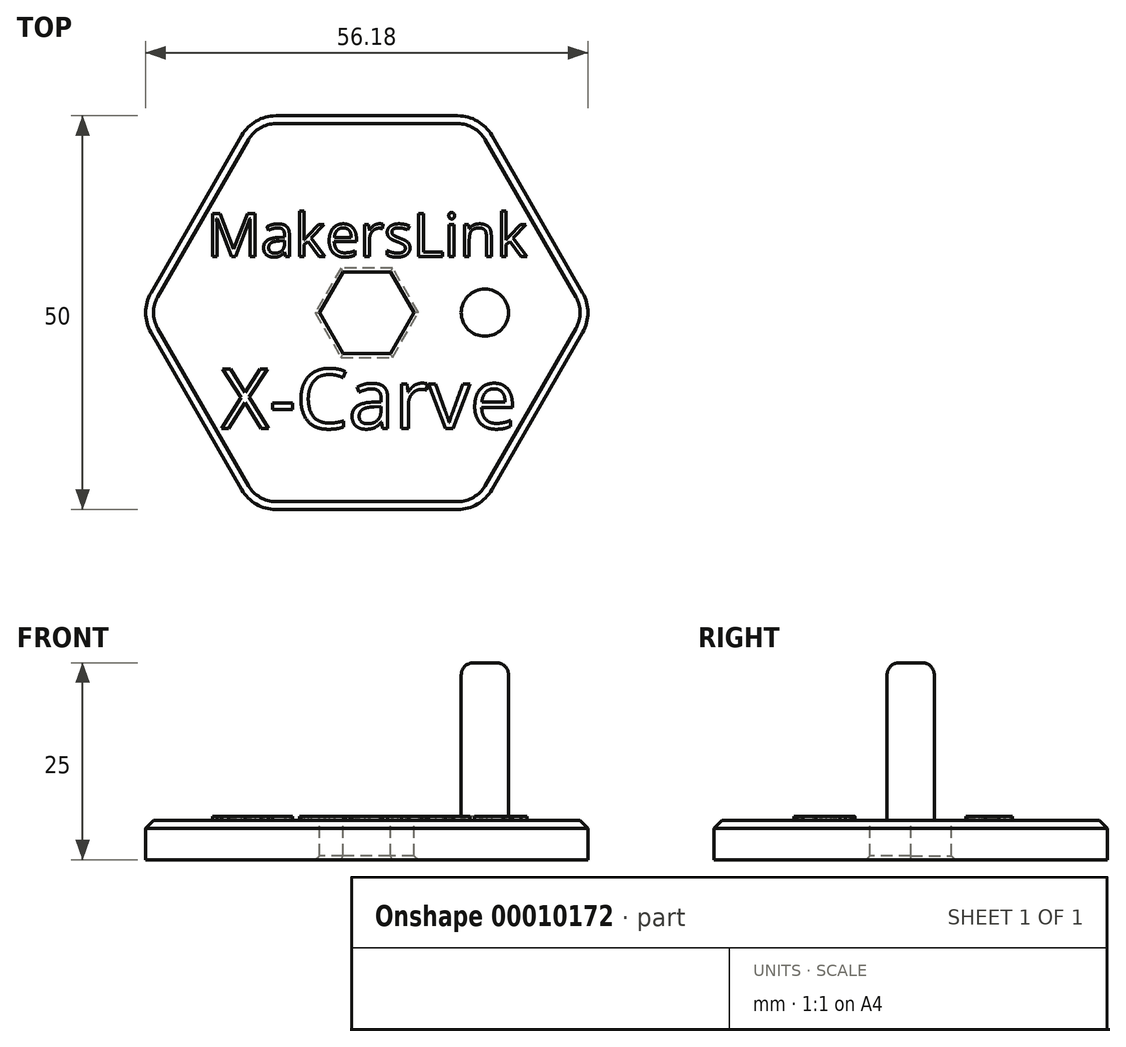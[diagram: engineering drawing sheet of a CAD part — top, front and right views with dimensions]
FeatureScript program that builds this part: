
annotation { "Feature Type Name" : "Feature", "Feature Type Description" : "" }
export const myFeature = defineFeature(function(context is Context, id is Id, definition is map)
    precondition{}
    {
        {
            var Q0;
            Q0=qCreatedBy(makeId("Top.planeOp"),FACE);
            var sketch = newSketch(context, id + "F0", { "sketchPlane" : qUnion([Q0])});
            skCircle(sketch, "E0.cCircle", {"center": v(0, 0) * mm, "radius": 5.17 * mm, "construction": true});
            skLineSegment(sketch, "E0.0", {"start": v(2.99, -5.17) * mm, "end": v(-2.99, -5.17) * mm});
            skLineSegment(sketch, "E0.1", {"start": v(-2.99, -5.17) * mm, "end": v(-5.98, 0) * mm});
            skLineSegment(sketch, "E0.2", {"start": v(-5.98, 0) * mm, "end": v(-2.99, 5.18) * mm});
            skLineSegment(sketch, "E0.3", {"start": v(-2.99, 5.17) * mm, "end": v(2.99, 5.18) * mm});
            skLineSegment(sketch, "E0.4", {"start": v(2.99, 5.18) * mm, "end": v(5.98, 0) * mm});
            skLineSegment(sketch, "E0.5", {"start": v(5.98, 0) * mm, "end": v(2.99, -5.17) * mm});
            skPoint(sketch, "E0.0.midPoint", {"position": v(0, -5.17) * mm});
            skCircle(sketch, "E1.cCircle", {"center": v(0, 0) * mm, "radius": 25 * mm, "construction": true});
            skLineSegment(sketch, "E1.0", {"start": v(14.43, -25) * mm, "end": v(-14.43, -25) * mm});
            skLineSegment(sketch, "E1.1", {"start": v(-14.43, -25) * mm, "end": v(-28.87, 0) * mm});
            skLineSegment(sketch, "E1.2", {"start": v(-28.87, 0) * mm, "end": v(-14.43, 25) * mm});
            skLineSegment(sketch, "E1.3", {"start": v(-14.43, 25) * mm, "end": v(14.43, 25) * mm});
            skLineSegment(sketch, "E1.4", {"start": v(14.43, 25) * mm, "end": v(28.87, 0) * mm});
            skLineSegment(sketch, "E1.5", {"start": v(28.87, 0) * mm, "end": v(14.43, -25) * mm});
            skPoint(sketch, "E1.0.midPoint", {"position": v(0, -25) * mm});
            skSolve(sketch);
        }
        {
            var Q0;
            Q0 = qSketchRegion(id + "F0", true);
            extrude(context, id + "F1", {"entities" : qUnion([Q0]), "oppositeDirection" : true, "depth" : 5 * mm});
        }
        {
            var Q0;
            Q0=makeQuery(id+"F1.opExtrude","CAP_FACE",FACE,{"disambiguationData":[OSD([sQuery(id+"F0.wireOp",EDGE,"E0.0"),sQuery(id+"F0.wireOp",EDGE,"E0.1"),sQuery(id+"F0.wireOp",EDGE,"E0.2"),sQuery(id+"F0.wireOp",EDGE,"E0.3"),sQuery(id+"F0.wireOp",EDGE,"E0.4"),sQuery(id+"F0.wireOp",EDGE,"E0.5"),sQuery(id+"F0.wireOp",EDGE,"E1.0"),sQuery(id+"F0.wireOp",EDGE,"E1.1"),sQuery(id+"F0.wireOp",EDGE,"E1.2"),sQuery(id+"F0.wireOp",EDGE,"E1.3"),sQuery(id+"F0.wireOp",EDGE,"E1.4"),sQuery(id+"F0.wireOp",EDGE,"E1.5")])],"isStart":true});
            var sketch = newSketch(context, id + "F2", { "sketchPlane" : qUnion([Q0])});
            skText(sketch, "E2", { "text": "X-Carve", "fontName": "OpenSans-Regular.ttf"});
            skText(sketch, "E3", { "text": "MakersLink", "fontName": "OpenSans-Regular.ttf"});
            const initialGuessF2  = {"E2": [-0.0185, -0.01472, 1, 0, 0.0076], "E3": [-0.02036, 0.00712, 1, 0, 0.0055]};
            skSetInitialGuess(sketch, initialGuessF2);
            skSolve(sketch);
        }
        {
            var Q0;
            Q0 = qSketchRegion(id + "F2", true);
            extrude(context, id + "F3", {"entities" : qUnion([Q0]), "operationType" : NewBodyOperationType.ADD, "depth" : 0.5 * mm});
        }
        {
            var Q0;
            Q0=makeQuery(id+"F1.opExtrude","SWEPT_EDGE",EDGE,{"disambiguationData":[OSD([sQuery(id+"F0.wireOp",EDGE,"E1.3"),sQuery(id+"F0.wireOp",EDGE,"E1.4")])]});
            var Q1;
            Q1=makeQuery(id+"F1.opExtrude","SWEPT_EDGE",EDGE,{"disambiguationData":[OSD([sQuery(id+"F0.wireOp",EDGE,"E1.4"),sQuery(id+"F0.wireOp",EDGE,"E1.5")])]});
            var Q2;
            Q2=makeQuery(id+"F1.opExtrude","SWEPT_EDGE",EDGE,{"disambiguationData":[OSD([sQuery(id+"F0.wireOp",EDGE,"E1.0"),sQuery(id+"F0.wireOp",EDGE,"E1.5")])]});
            var Q3;
            Q3=makeQuery(id+"F1.opExtrude","SWEPT_EDGE",EDGE,{"disambiguationData":[OSD([sQuery(id+"F0.wireOp",EDGE,"E1.0"),sQuery(id+"F0.wireOp",EDGE,"E1.1")])]});
            var Q4;
            Q4=makeQuery(id+"F1.opExtrude","SWEPT_EDGE",EDGE,{"disambiguationData":[OSD([sQuery(id+"F0.wireOp",EDGE,"E1.1"),sQuery(id+"F0.wireOp",EDGE,"E1.2")])]});
            var Q5;
            Q5=makeQuery(id+"F1.opExtrude","SWEPT_EDGE",EDGE,{"disambiguationData":[OSD([sQuery(id+"F0.wireOp",EDGE,"E1.2"),sQuery(id+"F0.wireOp",EDGE,"E1.3")])]});
            fillet(context, id + "F4", {"entities" : qUnion([Q0, Q1, Q2, Q3, Q4, Q5]), "radius" : 5 * mm, "tangentPropagation" : true, "allowEdgeOverflow" : false});
        }
        {
            var Q0;
            Q0=makeQuery(id+"F1.opExtrude","CAP_EDGE",EDGE,{"disambiguationData":[OSD([sQuery(id+"F0.wireOp",EDGE,"E1.3")])],"isStart":true});
            var Q1;
            Q1=makeQuery(id+"F1.opExtrude","CAP_EDGE",EDGE,{"disambiguationData":[OSD([sQuery(id+"F0.wireOp",EDGE,"E1.2")])],"isStart":true});
            var Q2;
            Q2=makeQuery(id+"F1.opExtrude","CAP_EDGE",EDGE,{"disambiguationData":[OSD([sQuery(id+"F0.wireOp",EDGE,"E1.1")])],"isStart":true});
            var Q3;
            {var subQ0=sQuery(id+"F0.wireOp",EDGE,"E1.1");var subQ1=sQuery(id+"F0.wireOp",EDGE,"E1.2");var subQ2=sQuery(id+"F0.wireOp",EDGE,"E0.0");var subQ3=sQuery(id+"F0.wireOp",EDGE,"E0.1");var subQ4=sQuery(id+"F0.wireOp",EDGE,"E0.2");var subQ5=sQuery(id+"F0.wireOp",EDGE,"E0.3");var subQ6=sQuery(id+"F0.wireOp",EDGE,"E0.4");var subQ7=sQuery(id+"F0.wireOp",EDGE,"E0.5");var subQ8=sQuery(id+"F0.wireOp",EDGE,"E1.0");var subQ9=sQuery(id+"F0.wireOp",EDGE,"E1.3");var subQ10=sQuery(id+"F0.wireOp",EDGE,"E1.4");var subQ11=sQuery(id+"F0.wireOp",EDGE,"E1.5");Q3=makeQuery(id+"F4.opFillet","BLEND_EDGE",EDGE,{"blendedFrom":[makeQuery(id+"F1.opExtrude","SWEPT_EDGE",EDGE,{"disambiguationData":[OSD([subQ0,subQ1])]}),makeQuery(id+"F3.boolean.opBoolean","SPLIT",FACE,{"disambiguationData":[TD([makeQuery(id+"F1.opExtrude","SWEPT_FACE",FACE,{"disambiguationData":[OSD([subQ2])]})])],"derivedFrom":makeQuery(id+"F1.opExtrude","CAP_FACE",FACE,{"disambiguationData":[OSD([subQ2,subQ3,subQ4,subQ5,subQ6,subQ7,subQ8,subQ0,subQ1,subQ9,subQ10,subQ11])],"isStart":true})})],"blendedInto":[makeQuery(id+"F3.boolean.opBoolean","SPLIT",FACE,{"disambiguationData":[TD([makeQuery(id+"F1.opExtrude","SWEPT_FACE",FACE,{"disambiguationData":[OSD([subQ2])]})])],"derivedFrom":makeQuery(id+"F1.opExtrude","CAP_FACE",FACE,{"disambiguationData":[OSD([subQ2,subQ3,subQ4,subQ5,subQ6,subQ7,subQ8,subQ0,subQ1,subQ9,subQ10,subQ11])],"isStart":true})})]});}
            var Q4;
            {var subQ0=sQuery(id+"F0.wireOp",EDGE,"E1.2");var subQ1=sQuery(id+"F0.wireOp",EDGE,"E1.3");var subQ2=sQuery(id+"F0.wireOp",EDGE,"E0.0");var subQ3=sQuery(id+"F0.wireOp",EDGE,"E0.1");var subQ4=sQuery(id+"F0.wireOp",EDGE,"E0.2");var subQ5=sQuery(id+"F0.wireOp",EDGE,"E0.3");var subQ6=sQuery(id+"F0.wireOp",EDGE,"E0.4");var subQ7=sQuery(id+"F0.wireOp",EDGE,"E0.5");var subQ8=sQuery(id+"F0.wireOp",EDGE,"E1.0");var subQ9=sQuery(id+"F0.wireOp",EDGE,"E1.1");var subQ10=sQuery(id+"F0.wireOp",EDGE,"E1.4");var subQ11=sQuery(id+"F0.wireOp",EDGE,"E1.5");Q4=makeQuery(id+"F4.opFillet","BLEND_EDGE",EDGE,{"blendedFrom":[makeQuery(id+"F1.opExtrude","SWEPT_EDGE",EDGE,{"disambiguationData":[OSD([subQ0,subQ1])]}),makeQuery(id+"F3.boolean.opBoolean","SPLIT",FACE,{"disambiguationData":[TD([makeQuery(id+"F1.opExtrude","SWEPT_FACE",FACE,{"disambiguationData":[OSD([subQ2])]})])],"derivedFrom":makeQuery(id+"F1.opExtrude","CAP_FACE",FACE,{"disambiguationData":[OSD([subQ2,subQ3,subQ4,subQ5,subQ6,subQ7,subQ8,subQ9,subQ0,subQ1,subQ10,subQ11])],"isStart":true})})],"blendedInto":[makeQuery(id+"F3.boolean.opBoolean","SPLIT",FACE,{"disambiguationData":[TD([makeQuery(id+"F1.opExtrude","SWEPT_FACE",FACE,{"disambiguationData":[OSD([subQ2])]})])],"derivedFrom":makeQuery(id+"F1.opExtrude","CAP_FACE",FACE,{"disambiguationData":[OSD([subQ2,subQ3,subQ4,subQ5,subQ6,subQ7,subQ8,subQ9,subQ0,subQ1,subQ10,subQ11])],"isStart":true})})]});}
            var Q5;
            {var subQ0=sQuery(id+"F0.wireOp",EDGE,"E1.3");var subQ1=sQuery(id+"F0.wireOp",EDGE,"E1.4");var subQ2=sQuery(id+"F0.wireOp",EDGE,"E0.0");var subQ3=sQuery(id+"F0.wireOp",EDGE,"E0.1");var subQ4=sQuery(id+"F0.wireOp",EDGE,"E0.2");var subQ5=sQuery(id+"F0.wireOp",EDGE,"E0.3");var subQ6=sQuery(id+"F0.wireOp",EDGE,"E0.4");var subQ7=sQuery(id+"F0.wireOp",EDGE,"E0.5");var subQ8=sQuery(id+"F0.wireOp",EDGE,"E1.0");var subQ9=sQuery(id+"F0.wireOp",EDGE,"E1.1");var subQ10=sQuery(id+"F0.wireOp",EDGE,"E1.2");var subQ11=sQuery(id+"F0.wireOp",EDGE,"E1.5");Q5=makeQuery(id+"F4.opFillet","BLEND_EDGE",EDGE,{"blendedFrom":[makeQuery(id+"F1.opExtrude","SWEPT_EDGE",EDGE,{"disambiguationData":[OSD([subQ0,subQ1])]}),makeQuery(id+"F3.boolean.opBoolean","SPLIT",FACE,{"disambiguationData":[TD([makeQuery(id+"F1.opExtrude","SWEPT_FACE",FACE,{"disambiguationData":[OSD([subQ2])]})])],"derivedFrom":makeQuery(id+"F1.opExtrude","CAP_FACE",FACE,{"disambiguationData":[OSD([subQ2,subQ3,subQ4,subQ5,subQ6,subQ7,subQ8,subQ9,subQ10,subQ0,subQ1,subQ11])],"isStart":true})})],"blendedInto":[makeQuery(id+"F3.boolean.opBoolean","SPLIT",FACE,{"disambiguationData":[TD([makeQuery(id+"F1.opExtrude","SWEPT_FACE",FACE,{"disambiguationData":[OSD([subQ2])]})])],"derivedFrom":makeQuery(id+"F1.opExtrude","CAP_FACE",FACE,{"disambiguationData":[OSD([subQ2,subQ3,subQ4,subQ5,subQ6,subQ7,subQ8,subQ9,subQ10,subQ0,subQ1,subQ11])],"isStart":true})})]});}
            var Q6;
            Q6=makeQuery(id+"F1.opExtrude","CAP_EDGE",EDGE,{"disambiguationData":[OSD([sQuery(id+"F0.wireOp",EDGE,"E1.4")])],"isStart":true});
            var Q7;
            {var subQ0=sQuery(id+"F0.wireOp",EDGE,"E1.4");var subQ1=sQuery(id+"F0.wireOp",EDGE,"E1.5");var subQ2=sQuery(id+"F0.wireOp",EDGE,"E0.0");var subQ3=sQuery(id+"F0.wireOp",EDGE,"E0.1");var subQ4=sQuery(id+"F0.wireOp",EDGE,"E0.2");var subQ5=sQuery(id+"F0.wireOp",EDGE,"E0.3");var subQ6=sQuery(id+"F0.wireOp",EDGE,"E0.4");var subQ7=sQuery(id+"F0.wireOp",EDGE,"E0.5");var subQ8=sQuery(id+"F0.wireOp",EDGE,"E1.0");var subQ9=sQuery(id+"F0.wireOp",EDGE,"E1.1");var subQ10=sQuery(id+"F0.wireOp",EDGE,"E1.2");var subQ11=sQuery(id+"F0.wireOp",EDGE,"E1.3");Q7=makeQuery(id+"F4.opFillet","BLEND_EDGE",EDGE,{"blendedFrom":[makeQuery(id+"F1.opExtrude","SWEPT_EDGE",EDGE,{"disambiguationData":[OSD([subQ0,subQ1])]}),makeQuery(id+"F3.boolean.opBoolean","SPLIT",FACE,{"disambiguationData":[TD([makeQuery(id+"F1.opExtrude","SWEPT_FACE",FACE,{"disambiguationData":[OSD([subQ2])]})])],"derivedFrom":makeQuery(id+"F1.opExtrude","CAP_FACE",FACE,{"disambiguationData":[OSD([subQ2,subQ3,subQ4,subQ5,subQ6,subQ7,subQ8,subQ9,subQ10,subQ11,subQ0,subQ1])],"isStart":true})})],"blendedInto":[makeQuery(id+"F3.boolean.opBoolean","SPLIT",FACE,{"disambiguationData":[TD([makeQuery(id+"F1.opExtrude","SWEPT_FACE",FACE,{"disambiguationData":[OSD([subQ2])]})])],"derivedFrom":makeQuery(id+"F1.opExtrude","CAP_FACE",FACE,{"disambiguationData":[OSD([subQ2,subQ3,subQ4,subQ5,subQ6,subQ7,subQ8,subQ9,subQ10,subQ11,subQ0,subQ1])],"isStart":true})})]});}
            var Q8;
            Q8=makeQuery(id+"F1.opExtrude","CAP_EDGE",EDGE,{"disambiguationData":[OSD([sQuery(id+"F0.wireOp",EDGE,"E1.5")])],"isStart":true});
            var Q9;
            {var subQ0=sQuery(id+"F0.wireOp",EDGE,"E1.0");var subQ1=sQuery(id+"F0.wireOp",EDGE,"E1.5");var subQ2=sQuery(id+"F0.wireOp",EDGE,"E0.0");var subQ3=sQuery(id+"F0.wireOp",EDGE,"E0.1");var subQ4=sQuery(id+"F0.wireOp",EDGE,"E0.2");var subQ5=sQuery(id+"F0.wireOp",EDGE,"E0.3");var subQ6=sQuery(id+"F0.wireOp",EDGE,"E0.4");var subQ7=sQuery(id+"F0.wireOp",EDGE,"E0.5");var subQ8=sQuery(id+"F0.wireOp",EDGE,"E1.1");var subQ9=sQuery(id+"F0.wireOp",EDGE,"E1.2");var subQ10=sQuery(id+"F0.wireOp",EDGE,"E1.3");var subQ11=sQuery(id+"F0.wireOp",EDGE,"E1.4");Q9=makeQuery(id+"F4.opFillet","BLEND_EDGE",EDGE,{"blendedFrom":[makeQuery(id+"F1.opExtrude","SWEPT_EDGE",EDGE,{"disambiguationData":[OSD([subQ0,subQ1])]}),makeQuery(id+"F3.boolean.opBoolean","SPLIT",FACE,{"disambiguationData":[TD([makeQuery(id+"F1.opExtrude","SWEPT_FACE",FACE,{"disambiguationData":[OSD([subQ2])]})])],"derivedFrom":makeQuery(id+"F1.opExtrude","CAP_FACE",FACE,{"disambiguationData":[OSD([subQ2,subQ3,subQ4,subQ5,subQ6,subQ7,subQ0,subQ8,subQ9,subQ10,subQ11,subQ1])],"isStart":true})})],"blendedInto":[makeQuery(id+"F3.boolean.opBoolean","SPLIT",FACE,{"disambiguationData":[TD([makeQuery(id+"F1.opExtrude","SWEPT_FACE",FACE,{"disambiguationData":[OSD([subQ2])]})])],"derivedFrom":makeQuery(id+"F1.opExtrude","CAP_FACE",FACE,{"disambiguationData":[OSD([subQ2,subQ3,subQ4,subQ5,subQ6,subQ7,subQ0,subQ8,subQ9,subQ10,subQ11,subQ1])],"isStart":true})})]});}
            var Q10;
            Q10=makeQuery(id+"F1.opExtrude","CAP_EDGE",EDGE,{"disambiguationData":[OSD([sQuery(id+"F0.wireOp",EDGE,"E1.0")])],"isStart":true});
            var Q11;
            {var subQ0=sQuery(id+"F0.wireOp",EDGE,"E1.0");var subQ1=sQuery(id+"F0.wireOp",EDGE,"E1.1");var subQ2=sQuery(id+"F0.wireOp",EDGE,"E0.0");var subQ3=sQuery(id+"F0.wireOp",EDGE,"E0.1");var subQ4=sQuery(id+"F0.wireOp",EDGE,"E0.2");var subQ5=sQuery(id+"F0.wireOp",EDGE,"E0.3");var subQ6=sQuery(id+"F0.wireOp",EDGE,"E0.4");var subQ7=sQuery(id+"F0.wireOp",EDGE,"E0.5");var subQ8=sQuery(id+"F0.wireOp",EDGE,"E1.2");var subQ9=sQuery(id+"F0.wireOp",EDGE,"E1.3");var subQ10=sQuery(id+"F0.wireOp",EDGE,"E1.4");var subQ11=sQuery(id+"F0.wireOp",EDGE,"E1.5");Q11=makeQuery(id+"F4.opFillet","BLEND_EDGE",EDGE,{"blendedFrom":[makeQuery(id+"F1.opExtrude","SWEPT_EDGE",EDGE,{"disambiguationData":[OSD([subQ0,subQ1])]}),makeQuery(id+"F3.boolean.opBoolean","SPLIT",FACE,{"disambiguationData":[TD([makeQuery(id+"F1.opExtrude","SWEPT_FACE",FACE,{"disambiguationData":[OSD([subQ2])]})])],"derivedFrom":makeQuery(id+"F1.opExtrude","CAP_FACE",FACE,{"disambiguationData":[OSD([subQ2,subQ3,subQ4,subQ5,subQ6,subQ7,subQ0,subQ1,subQ8,subQ9,subQ10,subQ11])],"isStart":true})})],"blendedInto":[makeQuery(id+"F3.boolean.opBoolean","SPLIT",FACE,{"disambiguationData":[TD([makeQuery(id+"F1.opExtrude","SWEPT_FACE",FACE,{"disambiguationData":[OSD([subQ2])]})])],"derivedFrom":makeQuery(id+"F1.opExtrude","CAP_FACE",FACE,{"disambiguationData":[OSD([subQ2,subQ3,subQ4,subQ5,subQ6,subQ7,subQ0,subQ1,subQ8,subQ9,subQ10,subQ11])],"isStart":true})})]});}
            chamfer(context, id + "F5", {"entities" : qUnion([Q0, Q1, Q2, Q3, Q4, Q5, Q6, Q7, Q8, Q9, Q10, Q11]), "width" : 1 * mm, "tangentPropagation" : true});
        }
        {
            var Q0;
            Q0=makeQuery(id+"F1.opExtrude","CAP_EDGE",EDGE,{"disambiguationData":[OSD([sQuery(id+"F0.wireOp",EDGE,"E0.5")])],"isStart":false});
            var Q1;
            Q1=makeQuery(id+"F1.opExtrude","CAP_EDGE",EDGE,{"disambiguationData":[OSD([sQuery(id+"F0.wireOp",EDGE,"E0.0")])],"isStart":false});
            var Q2;
            Q2=makeQuery(id+"F1.opExtrude","CAP_EDGE",EDGE,{"disambiguationData":[OSD([sQuery(id+"F0.wireOp",EDGE,"E0.1")])],"isStart":false});
            var Q3;
            Q3=makeQuery(id+"F1.opExtrude","CAP_EDGE",EDGE,{"disambiguationData":[OSD([sQuery(id+"F0.wireOp",EDGE,"E0.2")])],"isStart":false});
            var Q4;
            Q4=makeQuery(id+"F1.opExtrude","CAP_EDGE",EDGE,{"disambiguationData":[OSD([sQuery(id+"F0.wireOp",EDGE,"E0.3")])],"isStart":false});
            var Q5;
            Q5=makeQuery(id+"F1.opExtrude","CAP_EDGE",EDGE,{"disambiguationData":[OSD([sQuery(id+"F0.wireOp",EDGE,"E0.4")])],"isStart":false});
            chamfer(context, id + "F6", {"entities" : qUnion([Q0, Q1, Q2, Q3, Q4, Q5]), "width" : 0.5 * mm, "tangentPropagation" : true});
        }
        {
            var Q0;
            {var subQ0=sQuery(id+"F0.wireOp",EDGE,"E0.0");var subQ1=sQuery(id+"F0.wireOp",EDGE,"E0.1");var subQ2=sQuery(id+"F0.wireOp",EDGE,"E0.2");var subQ3=sQuery(id+"F0.wireOp",EDGE,"E0.3");var subQ4=sQuery(id+"F0.wireOp",EDGE,"E0.4");var subQ5=sQuery(id+"F0.wireOp",EDGE,"E0.5");var subQ6=sQuery(id+"F0.wireOp",EDGE,"E1.0");var subQ7=sQuery(id+"F0.wireOp",EDGE,"E1.1");var subQ8=sQuery(id+"F0.wireOp",EDGE,"E1.2");var subQ9=sQuery(id+"F0.wireOp",EDGE,"E1.3");var subQ10=sQuery(id+"F0.wireOp",EDGE,"E1.4");var subQ11=sQuery(id+"F0.wireOp",EDGE,"E1.5");Q0=makeQuery(id+"F3.boolean.opBoolean","SPLIT",FACE,{"disambiguationData":[TD([makeQuery(id+"F1.opExtrude","SWEPT_FACE",FACE,{"disambiguationData":[OSD([subQ0])]})])],"derivedFrom":makeQuery(id+"F1.opExtrude","CAP_FACE",FACE,{"disambiguationData":[OSD([subQ0,subQ1,subQ2,subQ3,subQ4,subQ5,subQ6,subQ7,subQ8,subQ9,subQ10,subQ11])],"isStart":true})});}
            var sketch = newSketch(context, id + "F7", { "sketchPlane" : qUnion([Q0])});
            skCircle(sketch, "E4", {"center": v(15, 0) * mm, "radius": 3 * mm});
            skSolve(sketch);
        }
        {
            var Q0;
            Q0 = qSketchRegion(id + "F7", true);
            extrude(context, id + "F8", {"entities" : qUnion([Q0]), "operationType" : NewBodyOperationType.ADD, "depth" : 20 * mm});
        }
        {
            var Q0;
            Q0=makeQuery(id+"F8.opExtrude","CAP_EDGE",EDGE,{"disambiguationData":[OSD([sQuery(id+"F7.wireOp",EDGE,"E4")])],"isStart":false});
            fillet(context, id + "F9", {"entities" : qUnion([Q0]), "radius" : 1.5 * mm, "tangentPropagation" : true, "allowEdgeOverflow" : false});
        }
    });
